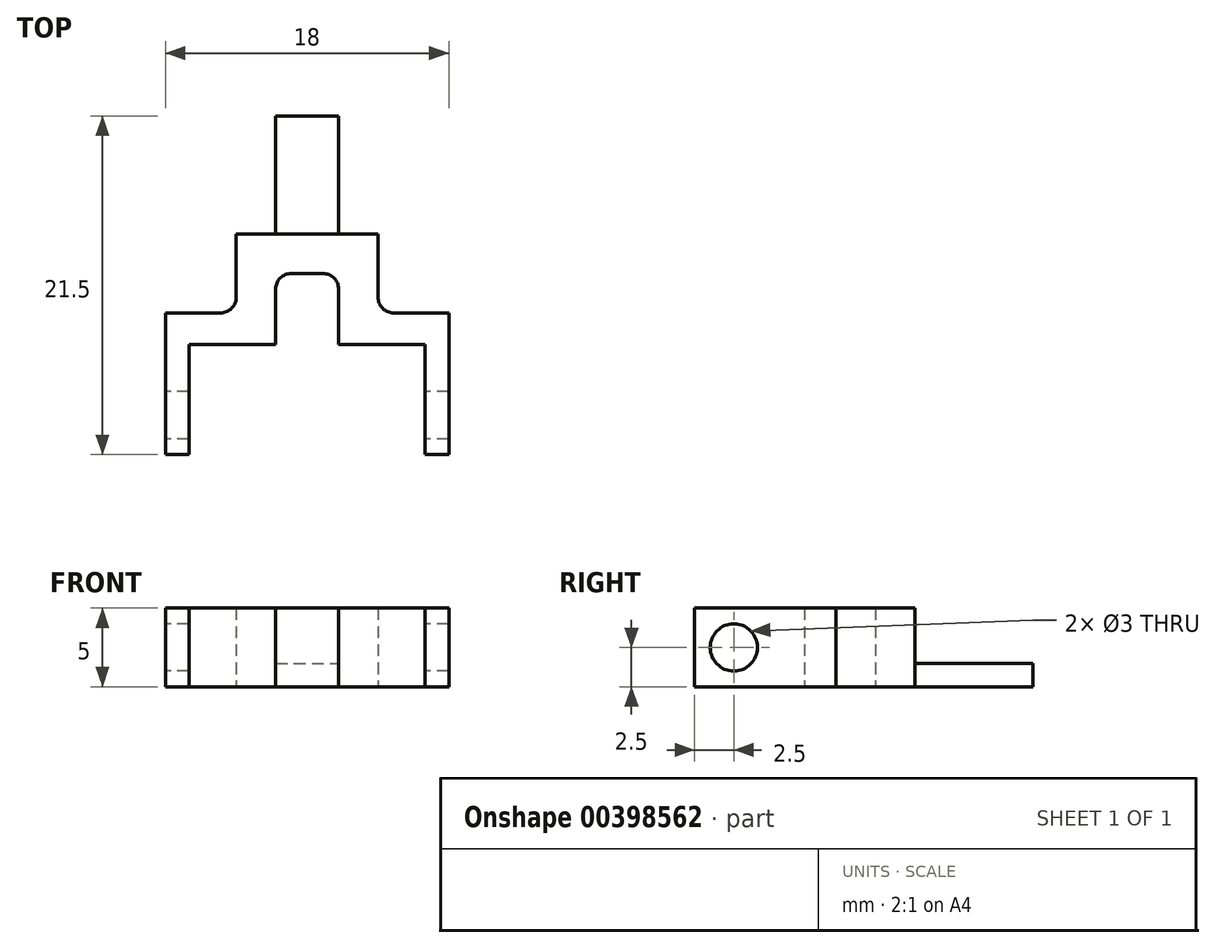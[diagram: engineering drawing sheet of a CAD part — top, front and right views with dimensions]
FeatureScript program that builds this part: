
annotation { "Feature Type Name" : "Feature", "Feature Type Description" : "" }
export const myFeature = defineFeature(function(context is Context, id is Id, definition is map)
    precondition{}
    {
        {
            var Q0;
            Q0=qCreatedBy(makeId("Top.planeOp"),FACE);
            var sketch = newSketch(context, id + "F0", { "sketchPlane" : qUnion([Q0])});
            skLineSegment(sketch, "E0.top", {"start": v(2, 5) * mm, "end": v(-2, 5) * mm});
            skLineSegment(sketch, "E0.left", {"start": v(2, -2.5) * mm, "end": v(2, 5) * mm});
            skLineSegment(sketch, "E0.right", {"start": v(-2, -2.5) * mm, "end": v(-2, 5) * mm});
            skPoint(sketch, "E0.middle", {"position": v(0, 0) * mm});
            skLineSegment(sketch, "E1.top", {"start": v(4.5, -2.5) * mm, "end": v(2, -2.5) * mm});
            skLineSegment(sketch, "E1.left", {"start": v(4.5, -7.5) * mm, "end": v(4.5, -2.5) * mm});
            skLineSegment(sketch, "E1.right", {"start": v(-4.5, -7.5) * mm, "end": v(-4.5, -2.5) * mm});
            skPoint(sketch, "E1.middle", {"position": v(0, -5) * mm});
            skLineSegment(sketch, "E2.bottom", {"start": v(-9, -7.5) * mm, "end": v(-4.5, -7.5) * mm});
            skLineSegment(sketch, "E2.top", {"start": v(-7.5, -9.5) * mm, "end": v(-2, -9.5) * mm});
            skLineSegment(sketch, "E2.left", {"start": v(-9, -7.5) * mm, "end": v(-9, -9.5) * mm});
            skLineSegment(sketch, "E2.right", {"start": v(9, -7.5) * mm, "end": v(9, -9.5) * mm});
            skLineSegment(sketch, "E3.top", {"start": v(-9, -16.5) * mm, "end": v(-7.5, -16.5) * mm});
            skLineSegment(sketch, "E3.left", {"start": v(-9, -9.5) * mm, "end": v(-9, -16.5) * mm});
            skLineSegment(sketch, "E3.right", {"start": v(-7.5, -9.5) * mm, "end": v(-7.5, -16.5) * mm});
            skLineSegment(sketch, "E4.top", {"start": v(9, -16.5) * mm, "end": v(7.5, -16.5) * mm});
            skLineSegment(sketch, "E4.left", {"start": v(9, -9.5) * mm, "end": v(9, -16.5) * mm});
            skLineSegment(sketch, "E4.right", {"start": v(7.5, -9.5) * mm, "end": v(7.5, -16.5) * mm});
            skLineSegment(sketch, "E5.trimOffspring", {"start": v(4.5, -7.5) * mm, "end": v(9, -7.5) * mm});
            skPoint(sketch, "E6.orphan", {"position": v(2, -5) * mm});
            skPoint(sketch, "E7.orphan", {"position": v(-2, -5) * mm});
            skLineSegment(sketch, "E8.trimOffspring", {"start": v(-2, -2.5) * mm, "end": v(-4.5, -2.5) * mm});
            skLineSegment(sketch, "E9", {"start": v(2, -2.5) * mm, "end": v(-2, -2.5) * mm});
            skLineSegment(sketch, "E10.bottom", {"start": v(-2, -5) * mm, "end": v(2, -5) * mm});
            skLineSegment(sketch, "E10.left", {"start": v(-2, -5) * mm, "end": v(-2, -9.5) * mm});
            skLineSegment(sketch, "E10.right", {"start": v(2, -5) * mm, "end": v(2, -9.5) * mm});
            skLineSegment(sketch, "E11.trimOffspring", {"start": v(2, -9.5) * mm, "end": v(7.5, -9.5) * mm});
            skSolve(sketch);
        }
        {
            var Q0;
            Q0 = qSketchRegion(id + "F0", true);
            extrude(context, id + "F1", {"entities" : qUnion([Q0]), "depth" : 1.5 * mm});
        }
        {
            var Q0;
            Q0=makeQuery(id+"F0.imprint","IMPRINT",FACE,{"disambiguationData":[TD([[makeQuery(id+"F0.imprint","IMPRINT",EDGE,{"derivedFrom":sQuery(id+"F0.wireOp",EDGE,"E1.top")}),1.0]])]});
            extrude(context, id + "F2", {"entities" : qUnion([Q0]), "operationType" : NewBodyOperationType.ADD, "depth" : 5 * mm});
        }
        {
            var Q0;
            {var subQ0=sQuery(id+"F0.wireOp",EDGE,"E3.left");var subQ1=sQuery(id+"F0.wireOp",EDGE,"E2.left");Q0=makeQuery(id+"F2.boolean.opBoolean","MERGE",FACE,{"derivedFrom":[makeQuery(id+"F1.opExtrude","SWEPT_FACE",FACE,{"disambiguationData":[OSD([subQ1,subQ0])]}),makeQuery(id+"F2.opExtrude","SWEPT_FACE",FACE,{"disambiguationData":[OSD([subQ1,subQ0])]})]});}
            var sketch = newSketch(context, id + "F3", { "sketchPlane" : qUnion([Q0])});
            skPoint(sketch, "E12", {"position": v(14, 2.5) * mm});
            skPoint(sketch, "E12.positionSnap0", {"position": v(16.5, 2.5) * mm});
            skCircle(sketch, "E13", {"center": v(14, 2.5) * mm, "radius": 1.5 * mm});
            skSolve(sketch);
        }
        {
            var Q0;
            Q0=sQuery(id+"F3.wireOp",VERTEX,"E12");
            var Q1;
            Q1=makeQuery(id+"F1.opExtrude","SWEPT_BODY",BODY,{"disambiguationData":[OSD([sQuery(id+"F0.wireOp",EDGE,"E0.top"),sQuery(id+"F0.wireOp",EDGE,"E0.left"),sQuery(id+"F0.wireOp",EDGE,"E0.right"),sQuery(id+"F0.wireOp",EDGE,"E1.top"),sQuery(id+"F0.wireOp",EDGE,"E1.left"),sQuery(id+"F0.wireOp",EDGE,"E1.right"),sQuery(id+"F0.wireOp",EDGE,"E2.bottom"),sQuery(id+"F0.wireOp",EDGE,"E2.top"),sQuery(id+"F0.wireOp",EDGE,"E2.left"),sQuery(id+"F0.wireOp",EDGE,"E2.right"),sQuery(id+"F0.wireOp",EDGE,"E3.top"),sQuery(id+"F0.wireOp",EDGE,"E3.left"),sQuery(id+"F0.wireOp",EDGE,"E3.right"),sQuery(id+"F0.wireOp",EDGE,"E4.top"),sQuery(id+"F0.wireOp",EDGE,"E4.left"),sQuery(id+"F0.wireOp",EDGE,"E4.right"),sQuery(id+"F0.wireOp",EDGE,"E5.trimOffspring"),sQuery(id+"F0.wireOp",EDGE,"E8.trimOffspring"),sQuery(id+"F0.wireOp",EDGE,"E10.bottom"),sQuery(id+"F0.wireOp",EDGE,"E10.left"),sQuery(id+"F0.wireOp",EDGE,"E10.right"),sQuery(id+"F0.wireOp",EDGE,"E11.trimOffspring")])]});
            hole(context, id + "F4", {"style" : HoleStyle.SIMPLE, "endStyle" : HoleEndStyle.THROUGH, "holeDiameter" : 3 * mm, "isTappedThrough" : true, "tappedDepth" : 12 * mm, "tapClearance" : 3, "locations" : qUnion([Q0]), "scope" : qUnion([Q1])});
        }
        {
            var Q0;
            {var subQ0=sQuery(id+"F0.wireOp",EDGE,"E10.right");var subQ1=sQuery(id+"F0.wireOp",EDGE,"E10.bottom");Q0=makeQuery(id+"F2.boolean.opBoolean","MERGE",EDGE,{"derivedFrom":[makeQuery(id+"F1.opExtrude","SWEPT_EDGE",EDGE,{"disambiguationData":[OSD([subQ1,subQ0])]}),makeQuery(id+"F2.opExtrude","SWEPT_EDGE",EDGE,{"disambiguationData":[OSD([subQ1,subQ0])]})]});}
            var Q1;
            {var subQ0=sQuery(id+"F0.wireOp",EDGE,"E10.left");var subQ1=sQuery(id+"F0.wireOp",EDGE,"E10.bottom");Q1=makeQuery(id+"F2.boolean.opBoolean","MERGE",EDGE,{"derivedFrom":[makeQuery(id+"F1.opExtrude","SWEPT_EDGE",EDGE,{"disambiguationData":[OSD([subQ1,subQ0])]}),makeQuery(id+"F2.opExtrude","SWEPT_EDGE",EDGE,{"disambiguationData":[OSD([subQ1,subQ0])]})]});}
            var Q2;
            {var subQ0=sQuery(id+"F0.wireOp",EDGE,"E2.bottom");var subQ1=sQuery(id+"F0.wireOp",EDGE,"E1.right");Q2=makeQuery(id+"F2.boolean.opBoolean","MERGE",EDGE,{"derivedFrom":[makeQuery(id+"F1.opExtrude","SWEPT_EDGE",EDGE,{"disambiguationData":[OSD([subQ1,subQ0])]}),makeQuery(id+"F2.opExtrude","SWEPT_EDGE",EDGE,{"disambiguationData":[OSD([subQ1,subQ0])]})]});}
            var Q3;
            {var subQ0=sQuery(id+"F0.wireOp",EDGE,"E5.trimOffspring");var subQ1=sQuery(id+"F0.wireOp",EDGE,"E1.left");Q3=makeQuery(id+"F2.boolean.opBoolean","MERGE",EDGE,{"derivedFrom":[makeQuery(id+"F1.opExtrude","SWEPT_EDGE",EDGE,{"disambiguationData":[OSD([subQ1,subQ0])]}),makeQuery(id+"F2.opExtrude","SWEPT_EDGE",EDGE,{"disambiguationData":[OSD([subQ1,subQ0])]})]});}
            fillet(context, id + "F5", {"entities" : qUnion([Q0, Q1, Q2, Q3]), "radius" : 1 * mm, "tangentPropagation" : true, "allowEdgeOverflow" : false});
        }
    });
